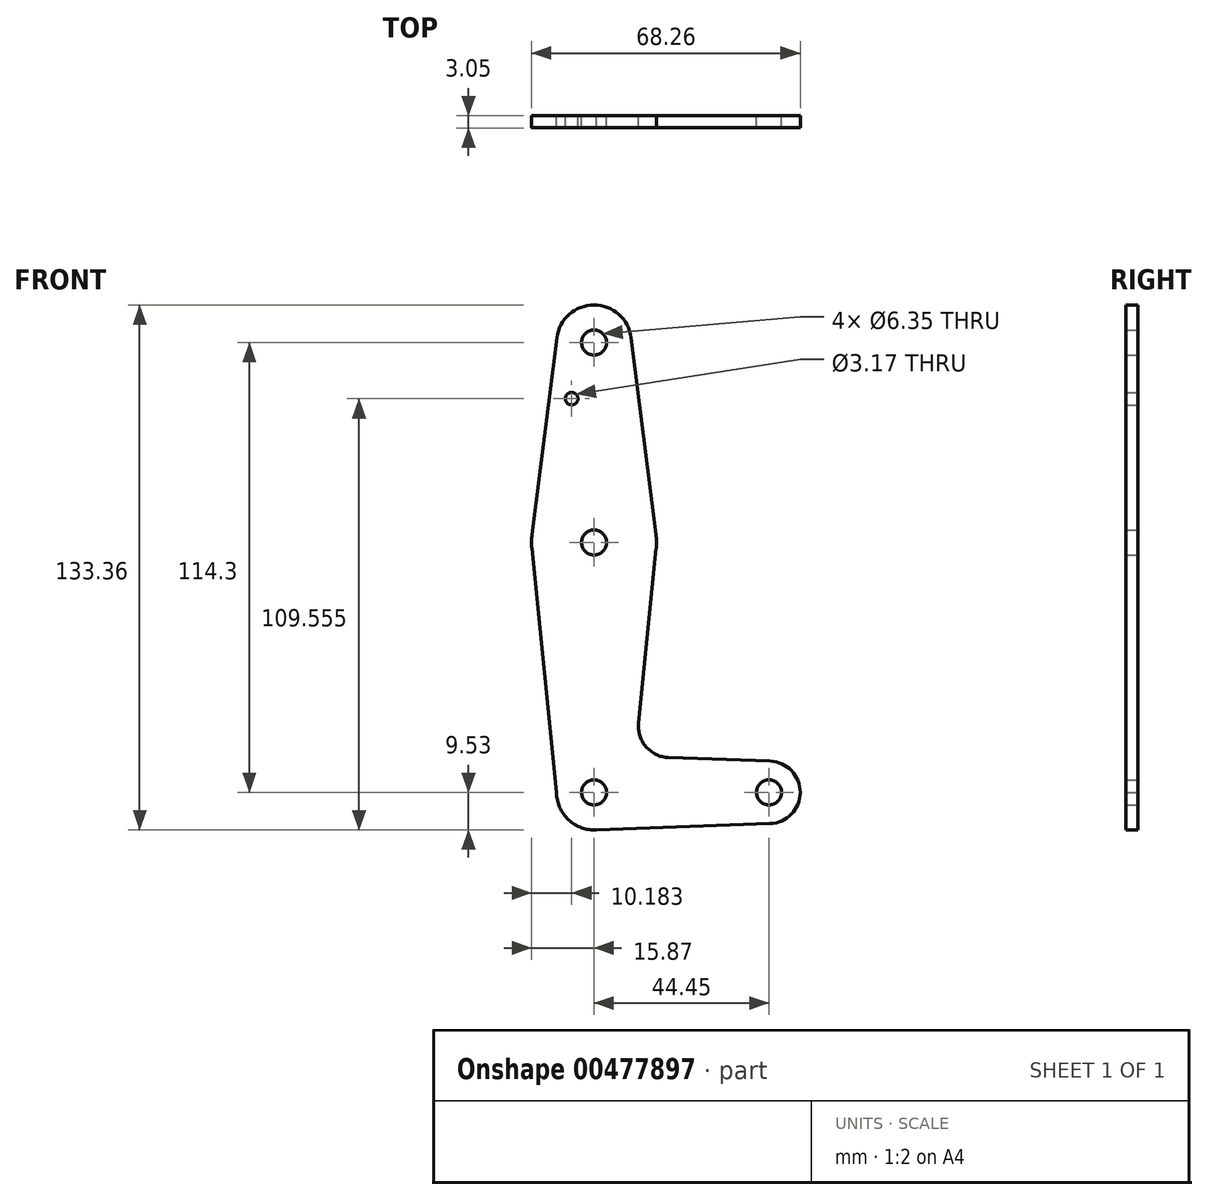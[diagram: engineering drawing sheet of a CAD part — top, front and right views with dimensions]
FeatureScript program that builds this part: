
annotation { "Feature Type Name" : "Feature", "Feature Type Description" : "" }
export const myFeature = defineFeature(function(context is Context, id is Id, definition is map)
    precondition{}
    {
        {
            var Q0;
            Q0=qCreatedBy(makeId("Front.planeOp"),FACE);
            var sketch = newSketch(context, id + "F0", { "sketchPlane" : qUnion([Q0])});
            skLineSegment(sketch, "E0", {"start": v(0, 114.3) * mm, "end": v(0, 0) * mm, "construction": true});
            skLineSegment(sketch, "E1", {"start": v(0, 0) * mm, "end": v(44.45, 0) * mm, "construction": true});
            skCircle(sketch, "E2", {"center": v(0, 114.3) * mm, "radius": 9.53 * mm});
            skCircle(sketch, "E3", {"center": v(0, 0) * mm, "radius": 9.53 * mm});
            skCircle(sketch, "E4", {"center": v(44.45, 0) * mm, "radius": 7.94 * mm});
            skCircle(sketch, "E5", {"center": v(0, 63.5) * mm, "radius": 15.88 * mm});
            skLineSegment(sketch, "E6", {"start": v(-9.45, 115.5) * mm, "end": v(-15.75, 65.48) * mm});
            skLineSegment(sketch, "E7", {"start": v(9.45, 115.5) * mm, "end": v(15.75, 65.48) * mm});
            skLineSegment(sketch, "E8", {"start": v(0, -9.53) * mm, "end": v(44.73, -7.93) * mm});
            skCircle(sketch, "E9", {"center": v(0, 114.3) * mm, "radius": 3.18 * mm});
            skCircle(sketch, "E10", {"center": v(0, 63.5) * mm, "radius": 3.18 * mm});
            skCircle(sketch, "E11", {"center": v(0, 0) * mm, "radius": 3.18 * mm});
            skCircle(sketch, "E12", {"center": v(44.45, 0) * mm, "radius": 3.18 * mm});
            skCircle(sketch, "E13", {"center": v(-5.69, 100.03) * mm, "radius": 1.59 * mm});
            skLineSegment(sketch, "E14", {"start": v(-9.53, 0) * mm, "end": v(-15.8, 61.9) * mm});
            skLineSegment(sketch, "E15", {"start": v(11.3, 17.6) * mm, "end": v(15.8, 61.9) * mm});
            skLineSegment(sketch, "E16", {"start": v(18.93, 8.85) * mm, "end": v(44.73, 7.93) * mm});
            skArc(sketch, "E17.filletArc", {"start": v(11.3, 17.6) * mm, "mid": v(13.22, 11.57) * mm, "end": v(18.93, 8.85) * mm});
            skSolve(sketch);
        }
        {
            var Q0;
            Q0 = qSketchRegion(id + "F0", true);
            extrude(context, id + "F1", {"entities" : qUnion([Q0]), "depth" : 3.05 * mm});
        }
    });
